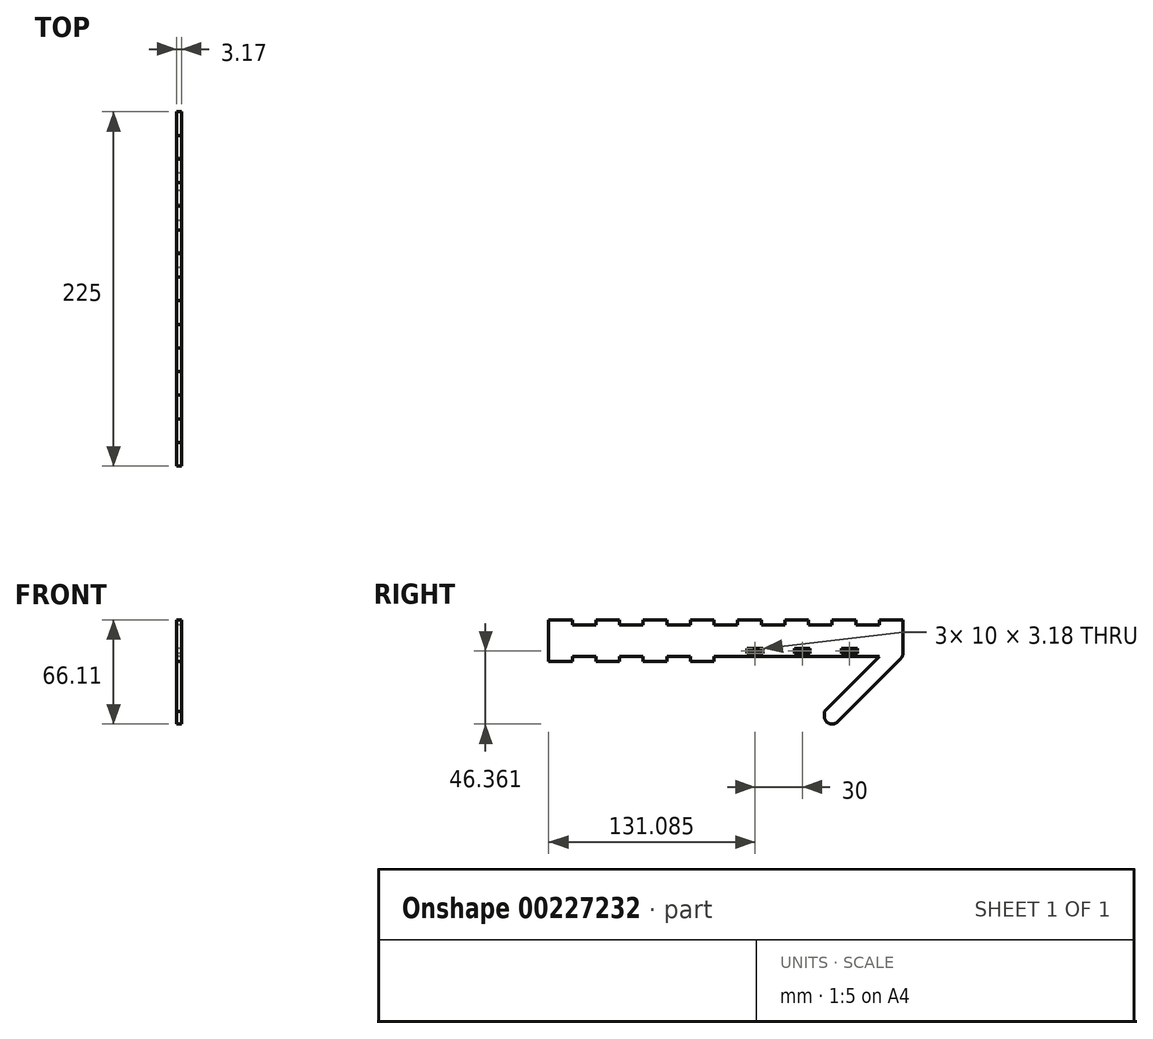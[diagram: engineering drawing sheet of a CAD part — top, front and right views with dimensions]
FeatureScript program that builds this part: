
annotation { "Feature Type Name" : "Feature", "Feature Type Description" : "" }
export const myFeature = defineFeature(function(context is Context, id is Id, definition is map)
    precondition{}
    {
        {
            var Q0;
            Q0=qCreatedBy(makeId("Right.planeOp"),FACE);
            var sketch = newSketch(context, id + "F0", { "sketchPlane" : qUnion([Q0])});
            skLineSegment(sketch, "E0.bottom", {"start": v(-101.54, 0) * mm, "end": v(108.46, 0) * mm});
            skLineSegment(sketch, "E0.top", {"start": v(-101.54, 20) * mm, "end": v(108.46, 20) * mm});
            skLineSegment(sketch, "E0.left", {"start": v(-101.54, 0) * mm, "end": v(-101.54, 20) * mm});
            skLineSegment(sketch, "E0.right", {"start": v(108.46, 0) * mm, "end": v(108.46, 20) * mm});
            skLineSegment(sketch, "E1", {"start": v(-101.54, 0) * mm, "end": v(-101.54, -3.17) * mm});
            skLineSegment(sketch, "E2", {"start": v(-101.54, -3.17) * mm, "end": v(-86.54, -3.17) * mm});
            skLineSegment(sketch, "E3", {"start": v(-86.54, -3.17) * mm, "end": v(-86.54, 0) * mm});
            skLineSegment(sketch, "E4.1.0.0", {"start": v(-71.54, -3.17) * mm, "end": v(-56.54, -3.17) * mm});
            skLineSegment(sketch, "E4.1.0.1", {"start": v(-56.54, -3.17) * mm, "end": v(-56.54, 0) * mm});
            skLineSegment(sketch, "E4.1.0.2", {"start": v(-71.54, 0) * mm, "end": v(-71.54, -3.17) * mm});
            skLineSegment(sketch, "E4.2.0.0", {"start": v(-41.54, -3.17) * mm, "end": v(-26.54, -3.17) * mm});
            skLineSegment(sketch, "E4.2.0.1", {"start": v(-26.54, -3.17) * mm, "end": v(-26.54, 0) * mm});
            skLineSegment(sketch, "E4.2.0.2", {"start": v(-41.54, 0) * mm, "end": v(-41.54, -3.17) * mm});
            skLineSegment(sketch, "E4.3.0.0", {"start": v(-11.54, -3.17) * mm, "end": v(3.46, -3.17) * mm});
            skLineSegment(sketch, "E4.3.0.1", {"start": v(3.46, -3.17) * mm, "end": v(3.46, 0) * mm});
            skLineSegment(sketch, "E4.3.0.2", {"start": v(-11.54, 0) * mm, "end": v(-11.54, -3.17) * mm});
            skLineSegment(sketch, "E4.direction1", {"start": v(-101.54, -3.17) * mm, "end": v(-71.54, -3.17) * mm, "construction": true});
            skLineSegment(sketch, "E5.bottom", {"start": v(34.55, 1.84) * mm, "end": v(24.55, 1.84) * mm});
            skLineSegment(sketch, "E5.top", {"start": v(34.55, 5.02) * mm, "end": v(24.55, 5.02) * mm});
            skLineSegment(sketch, "E5.left", {"start": v(34.55, 1.84) * mm, "end": v(34.55, 5.02) * mm});
            skLineSegment(sketch, "E5.right", {"start": v(24.55, 1.84) * mm, "end": v(24.55, 5.02) * mm});
            skPoint(sketch, "E5.middle", {"position": v(29.55, 3.43) * mm});
            skPoint(sketch, "E6.1.0.0", {"position": v(59.55, 2.84) * mm});
            skLineSegment(sketch, "E6.1.0.1", {"start": v(64.55, 1.84) * mm, "end": v(64.55, 5.02) * mm});
            skLineSegment(sketch, "E6.1.0.2", {"start": v(64.55, 1.84) * mm, "end": v(54.55, 1.84) * mm});
            skLineSegment(sketch, "E6.1.0.3", {"start": v(64.55, 5.02) * mm, "end": v(54.55, 5.02) * mm});
            skLineSegment(sketch, "E6.1.0.4", {"start": v(54.55, 1.84) * mm, "end": v(54.55, 5.02) * mm});
            skLineSegment(sketch, "E6.direction1", {"start": v(24.55, 1.84) * mm, "end": v(54.55, 1.84) * mm, "construction": true});
            skLineSegment(sketch, "E7.bottom", {"start": v(73.46, 0) * mm, "end": v(38.04, 0) * mm});
            skLineSegment(sketch, "E7.left", {"start": v(73.46, 0) * mm, "end": v(73.46, -50) * mm});
            skLineSegment(sketch, "E8.bottom", {"start": v(34.55, -15.92) * mm, "end": v(24.55, -15.92) * mm});
            skLineSegment(sketch, "E8.top", {"start": v(34.55, -12.74) * mm, "end": v(24.55, -12.74) * mm});
            skLineSegment(sketch, "E8.left", {"start": v(34.55, -15.92) * mm, "end": v(34.55, -12.74) * mm});
            skLineSegment(sketch, "E8.right", {"start": v(24.55, -15.92) * mm, "end": v(24.55, -12.74) * mm});
            skPoint(sketch, "E8.middle", {"position": v(29.55, -14.33) * mm});
            skLineSegment(sketch, "E9.0.1.0", {"start": v(35.55, -32.74) * mm, "end": v(24.55, -32.74) * mm});
            skLineSegment(sketch, "E9.0.1.1", {"start": v(35.55, -35.92) * mm, "end": v(24.55, -35.92) * mm});
            skLineSegment(sketch, "E9.0.1.2", {"start": v(35.55, -35.92) * mm, "end": v(35.55, -32.74) * mm});
            skLineSegment(sketch, "E9.0.1.3", {"start": v(24.55, -35.92) * mm, "end": v(24.55, -32.74) * mm});
            skLineSegment(sketch, "E9.direction2", {"start": v(24.55, -15.92) * mm, "end": v(24.55, -35.92) * mm, "construction": true});
            skLineSegment(sketch, "E10", {"start": v(73.46, -50) * mm, "end": v(21.5, -50) * mm});
            skLineSegment(sketch, "E11", {"start": v(21.5, -50) * mm, "end": v(21.5, 0) * mm});
            skPoint(sketch, "E12.1.0.0", {"position": v(59.55, -14.33) * mm});
            skLineSegment(sketch, "E12.1.0.1", {"start": v(65.55, -35.92) * mm, "end": v(65.55, -32.74) * mm});
            skLineSegment(sketch, "E12.1.0.2", {"start": v(64.55, -15.92) * mm, "end": v(54.55, -15.92) * mm});
            skLineSegment(sketch, "E12.1.0.3", {"start": v(65.55, -32.74) * mm, "end": v(54.55, -32.74) * mm});
            skLineSegment(sketch, "E12.1.0.4", {"start": v(64.55, -12.74) * mm, "end": v(54.55, -12.74) * mm});
            skLineSegment(sketch, "E12.1.0.5", {"start": v(64.55, -15.92) * mm, "end": v(64.55, -12.74) * mm});
            skLineSegment(sketch, "E12.1.0.6", {"start": v(65.55, -35.92) * mm, "end": v(54.55, -35.92) * mm});
            skLineSegment(sketch, "E12.1.0.7", {"start": v(54.55, -15.92) * mm, "end": v(54.55, -35.92) * mm, "construction": true});
            skLineSegment(sketch, "E12.1.0.8", {"start": v(54.55, -15.92) * mm, "end": v(54.55, -12.74) * mm});
            skLineSegment(sketch, "E12.1.0.9", {"start": v(54.55, -35.92) * mm, "end": v(54.55, -32.74) * mm});
            skLineSegment(sketch, "E12.direction1", {"start": v(24.55, -35.92) * mm, "end": v(54.55, -35.92) * mm, "construction": true});
            skPoint(sketch, "E13.0.2.0", {"position": v(89.55, 2.84) * mm});
            skLineSegment(sketch, "E13.1.2.0", {"start": v(94.55, 1.84) * mm, "end": v(94.55, 5.02) * mm});
            skLineSegment(sketch, "E13.4.2.0", {"start": v(94.55, 1.84) * mm, "end": v(84.55, 1.84) * mm});
            skLineSegment(sketch, "E13.7.2.0", {"start": v(94.55, 5.02) * mm, "end": v(84.55, 5.02) * mm});
            skLineSegment(sketch, "E13.10.2.0", {"start": v(84.55, 1.84) * mm, "end": v(84.55, 5.02) * mm});
            skLineSegment(sketch, "E14", {"start": v(-101.54, 20) * mm, "end": v(-101.54, 23.18) * mm});
            skLineSegment(sketch, "E15", {"start": v(-101.54, 23.18) * mm, "end": v(-86.54, 23.18) * mm});
            skLineSegment(sketch, "E16", {"start": v(-86.54, 23.18) * mm, "end": v(-86.54, 20) * mm});
            skLineSegment(sketch, "E17.1.0.0", {"start": v(-56.54, 23.18) * mm, "end": v(-56.54, 20) * mm});
            skLineSegment(sketch, "E17.1.0.1", {"start": v(-71.54, 23.18) * mm, "end": v(-56.54, 23.18) * mm});
            skLineSegment(sketch, "E17.1.0.2", {"start": v(-71.54, 20) * mm, "end": v(-71.54, 23.18) * mm});
            skLineSegment(sketch, "E17.2.0.0", {"start": v(-26.54, 23.18) * mm, "end": v(-26.54, 20) * mm});
            skLineSegment(sketch, "E17.2.0.1", {"start": v(-41.54, 23.18) * mm, "end": v(-26.54, 23.18) * mm});
            skLineSegment(sketch, "E17.2.0.2", {"start": v(-41.54, 20) * mm, "end": v(-41.54, 23.18) * mm});
            skLineSegment(sketch, "E17.3.0.0", {"start": v(3.46, 23.18) * mm, "end": v(3.46, 20) * mm});
            skLineSegment(sketch, "E17.3.0.1", {"start": v(-11.54, 23.18) * mm, "end": v(3.46, 23.18) * mm});
            skLineSegment(sketch, "E17.3.0.2", {"start": v(-11.54, 20) * mm, "end": v(-11.54, 23.18) * mm});
            skLineSegment(sketch, "E17.4.0.0", {"start": v(33.46, 23.18) * mm, "end": v(33.46, 20) * mm});
            skLineSegment(sketch, "E17.4.0.1", {"start": v(18.46, 23.18) * mm, "end": v(33.46, 23.18) * mm});
            skLineSegment(sketch, "E17.4.0.2", {"start": v(18.46, 20) * mm, "end": v(18.46, 23.18) * mm});
            skLineSegment(sketch, "E17.5.0.0", {"start": v(63.46, 23.18) * mm, "end": v(63.46, 20) * mm});
            skLineSegment(sketch, "E17.5.0.1", {"start": v(48.46, 23.18) * mm, "end": v(63.46, 23.18) * mm});
            skLineSegment(sketch, "E17.5.0.2", {"start": v(48.46, 20) * mm, "end": v(48.46, 23.18) * mm});
            skLineSegment(sketch, "E17.6.0.0", {"start": v(93.46, 23.18) * mm, "end": v(93.46, 20) * mm});
            skLineSegment(sketch, "E17.6.0.1", {"start": v(78.46, 23.18) * mm, "end": v(93.46, 23.18) * mm});
            skLineSegment(sketch, "E17.6.0.2", {"start": v(78.46, 20) * mm, "end": v(78.46, 23.18) * mm});
            skLineSegment(sketch, "E17.direction1", {"start": v(-86.54, 20) * mm, "end": v(-56.54, 20) * mm, "construction": true});
            skLineSegment(sketch, "E18", {"start": v(108.46, 20) * mm, "end": v(123.46, 20) * mm});
            skLineSegment(sketch, "E19", {"start": v(123.46, 20) * mm, "end": v(123.46, 23.18) * mm});
            skLineSegment(sketch, "E20", {"start": v(123.46, 23.18) * mm, "end": v(108.46, 23.18) * mm});
            skLineSegment(sketch, "E21", {"start": v(108.46, 23.18) * mm, "end": v(108.46, 20) * mm});
            skLineSegment(sketch, "E22", {"start": v(123.46, 20) * mm, "end": v(123.46, 0) * mm});
            skLineSegment(sketch, "E23", {"start": v(123.46, 0) * mm, "end": v(108.46, 0) * mm});
            skLineSegment(sketch, "E24", {"start": v(108.46, 0) * mm, "end": v(73.46, -35) * mm});
            skLineSegment(sketch, "E25", {"start": v(123.46, 0) * mm, "end": v(73.46, -50) * mm});
            skSolve(sketch);
        }
        {
            var Q0;
            {var subQ0=sQuery(id+"F0.wireOp",EDGE,"E1");Q0=makeQuery(id+"F0.imprint","IMPRINT",FACE,{"disambiguationData":[TD([[makeQuery(id+"F0.imprint","IMPRINT",EDGE,{"derivedFrom":subQ0}),1.0]])]});}
            var Q1;
            {var subQ0=sQuery(id+"F0.wireOp",EDGE,"E4.1.0.1");Q1=makeQuery(id+"F0.imprint","IMPRINT",FACE,{"disambiguationData":[TD([[makeQuery(id+"F0.imprint","IMPRINT",EDGE,{"derivedFrom":subQ0}),1.0]])]});}
            var Q2;
            {var subQ0=sQuery(id+"F0.wireOp",EDGE,"E4.2.0.1");Q2=makeQuery(id+"F0.imprint","IMPRINT",FACE,{"disambiguationData":[TD([[makeQuery(id+"F0.imprint","IMPRINT",EDGE,{"derivedFrom":subQ0}),1.0]])]});}
            var Q3;
            {var subQ0=sQuery(id+"F0.wireOp",EDGE,"E4.3.0.1");Q3=makeQuery(id+"F0.imprint","IMPRINT",FACE,{"disambiguationData":[TD([[makeQuery(id+"F0.imprint","IMPRINT",EDGE,{"derivedFrom":subQ0}),1.0]])]});}
            var Q4;
            Q4=makeQuery(id+"F0.imprint","IMPRINT",FACE,{"disambiguationData":[TD([[makeQuery(id+"F0.imprint","IMPRINT",EDGE,{"derivedFrom":sQuery(id+"F0.wireOp",EDGE,"ce93e1d3-3995-49a6-8b67-9a0789bbba461.MirrorCS")}),-1.0]])]});
            var Q5;
            {var subQ0=sQuery(id+"F0.wireOp",EDGE,"ce93e1d3-3995-49a6-8b67-9a0789bbba4610.MirrorCS");Q5=makeQuery(id+"F0.imprint","IMPRINT",FACE,{"disambiguationData":[TD([[makeQuery(id+"F0.imprint","IMPRINT",EDGE,{"derivedFrom":subQ0}),-1.0]])]});}
            var Q6;
            {var subQ0=sQuery(id+"F0.wireOp",EDGE,"ce93e1d3-3995-49a6-8b67-9a0789bbba467.MirrorCS");Q6=makeQuery(id+"F0.imprint","IMPRINT",FACE,{"disambiguationData":[TD([[makeQuery(id+"F0.imprint","IMPRINT",EDGE,{"derivedFrom":subQ0}),-1.0]])]});}
            var Q7;
            Q7=makeQuery(id+"F0.imprint","IMPRINT",FACE,{"disambiguationData":[TD([[makeQuery(id+"F0.imprint","IMPRINT",EDGE,{"derivedFrom":sQuery(id+"F0.wireOp",EDGE,"ce93e1d3-3995-49a6-8b67-9a0789bbba466.MirrorCS")}),-1.0]])]});
            var Q8;
            {var subQ0=sQuery(id+"F0.wireOp",EDGE,"2162bb09-abec-4cb4-a067-2c19ad6defc6.1.0.3");Q8=makeQuery(id+"F0.imprint","IMPRINT",FACE,{"disambiguationData":[TD([[makeQuery(id+"F0.imprint","IMPRINT",EDGE,{"derivedFrom":subQ0}),-1.0]])]});}
            var Q9;
            Q9=makeQuery(id+"F0.imprint","IMPRINT",FACE,{"disambiguationData":[TD([[makeQuery(id+"F0.imprint","IMPRINT",EDGE,{"derivedFrom":sQuery(id+"F0.wireOp",EDGE,"2162bb09-abec-4cb4-a067-2c19ad6defc6.1.0.2")}),-1.0]])]});
            var Q10;
            {var subQ0=sQuery(id+"F0.wireOp",EDGE,"188c20dd-d373-43bf-8d52-a3ebaf6e5f43.1.0.0");Q10=makeQuery(id+"F0.imprint","IMPRINT",FACE,{"disambiguationData":[TD([[makeQuery(id+"F0.imprint","IMPRINT",EDGE,{"derivedFrom":subQ0}),-1.0]])]});}
            var Q11;
            {var subQ0=sQuery(id+"F0.wireOp",EDGE,"E0.left");Q11=makeQuery(id+"F0.imprint","IMPRINT",FACE,{"disambiguationData":[TD([[makeQuery(id+"F0.imprint","IMPRINT",EDGE,{"derivedFrom":subQ0}),-1.0]])]});}
            var Q12;
            Q12=makeQuery(id+"F0.imprint","IMPRINT",FACE,{"disambiguationData":[TD([[makeQuery(id+"F0.imprint","IMPRINT",EDGE,{"derivedFrom":sQuery(id+"F0.wireOp",EDGE,"E7.bottom")}),1.0]])]});
            var Q13;
            {var subQ3=sQuery(id+"F0.wireOp",EDGE,"RmzYyfY4-P3xS-SvZ0-Tbu5-DnoCzGWXTxIq");Q13=makeQuery(id+"F0.imprint","IMPRINT",FACE,{"disambiguationData":[TD([[makeQuery(id+"F0.imprint","IMPRINT",EDGE,{"derivedFrom":subQ3}),1.0]])]});}
            var Q14;
            {var subQ0=sQuery(id+"F0.wireOp",EDGE,"E14");Q14=makeQuery(id+"F0.imprint","IMPRINT",FACE,{"disambiguationData":[TD([[makeQuery(id+"F0.imprint","IMPRINT",EDGE,{"derivedFrom":subQ0}),-1.0]])]});}
            var Q15;
            {var subQ0=sQuery(id+"F0.wireOp",EDGE,"E17.1.0.0");Q15=makeQuery(id+"F0.imprint","IMPRINT",FACE,{"disambiguationData":[TD([[makeQuery(id+"F0.imprint","IMPRINT",EDGE,{"derivedFrom":subQ0}),-1.0]])]});}
            var Q16;
            {var subQ0=sQuery(id+"F0.wireOp",EDGE,"E17.2.0.0");Q16=makeQuery(id+"F0.imprint","IMPRINT",FACE,{"disambiguationData":[TD([[makeQuery(id+"F0.imprint","IMPRINT",EDGE,{"derivedFrom":subQ0}),-1.0]])]});}
            var Q17;
            {var subQ0=sQuery(id+"F0.wireOp",EDGE,"E17.3.0.0");Q17=makeQuery(id+"F0.imprint","IMPRINT",FACE,{"disambiguationData":[TD([[makeQuery(id+"F0.imprint","IMPRINT",EDGE,{"derivedFrom":subQ0}),-1.0]])]});}
            var Q18;
            {var subQ0=sQuery(id+"F0.wireOp",EDGE,"E17.4.0.0");Q18=makeQuery(id+"F0.imprint","IMPRINT",FACE,{"disambiguationData":[TD([[makeQuery(id+"F0.imprint","IMPRINT",EDGE,{"derivedFrom":subQ0}),-1.0]])]});}
            var Q19;
            {var subQ0=sQuery(id+"F0.wireOp",EDGE,"E17.5.0.0");Q19=makeQuery(id+"F0.imprint","IMPRINT",FACE,{"disambiguationData":[TD([[makeQuery(id+"F0.imprint","IMPRINT",EDGE,{"derivedFrom":subQ0}),-1.0]])]});}
            var Q20;
            {var subQ0=sQuery(id+"F0.wireOp",EDGE,"E17.6.0.0");Q20=makeQuery(id+"F0.imprint","IMPRINT",FACE,{"disambiguationData":[TD([[makeQuery(id+"F0.imprint","IMPRINT",EDGE,{"derivedFrom":subQ0}),-1.0]])]});}
            var Q21;
            Q21=makeQuery(id+"F0.imprint","IMPRINT",FACE,{"disambiguationData":[TD([[makeQuery(id+"F0.imprint","IMPRINT",EDGE,{"derivedFrom":sQuery(id+"F0.wireOp",EDGE,"E18")}),1.0]])]});
            var Q22;
            Q22=makeQuery(id+"F0.imprint","IMPRINT",FACE,{"disambiguationData":[TD([[makeQuery(id+"F0.imprint","IMPRINT",EDGE,{"derivedFrom":sQuery(id+"F0.wireOp",EDGE,"E0.right")}),-1.0]])]});
            var Q23;
            Q23=makeQuery(id+"F0.imprint","IMPRINT",FACE,{"disambiguationData":[TD([[makeQuery(id+"F0.imprint","IMPRINT",EDGE,{"derivedFrom":sQuery(id+"F0.wireOp",EDGE,"E23")}),1.0]])]});
            extrude(context, id + "F1", {"entities" : qUnion([Q0, Q1, Q2, Q3, Q4, Q5, Q6, Q7, Q8, Q9, Q10, Q11, Q12, Q13, Q14, Q15, Q16, Q17, Q18, Q19, Q20, Q21, Q22, Q23]), "depth" : 3.17 * mm});
        }
        {
            var Q0;
            Q0=makeQuery(id+"F1.opExtrude","SWEPT_EDGE",EDGE,{"disambiguationData":[OSD([sQuery(id+"F0.wireOp",EDGE,"E22"),sQuery(id+"F0.wireOp",EDGE,"E23")])]});
            var Q1;
            Q1=makeQuery(id+"F1.opExtrude","SWEPT_EDGE",EDGE,{"disambiguationData":[OSD([sQuery(id+"F0.wireOp",EDGE,"E7.left"),sQuery(id+"F0.wireOp",EDGE,"E10")])]});
            var Q2;
            Q2=makeQuery(id+"F1.opExtrude","SWEPT_EDGE",EDGE,{"disambiguationData":[OSD([sQuery(id+"F0.wireOp",EDGE,"E10"),sQuery(id+"F0.wireOp",EDGE,"E11")])]});
            fillet(context, id + "F2", {"entities" : qUnion([Q0, Q1, Q2]), "radius" : 5 * mm, "tangentPropagation" : true, "allowEdgeOverflow" : false});
        }
    });
